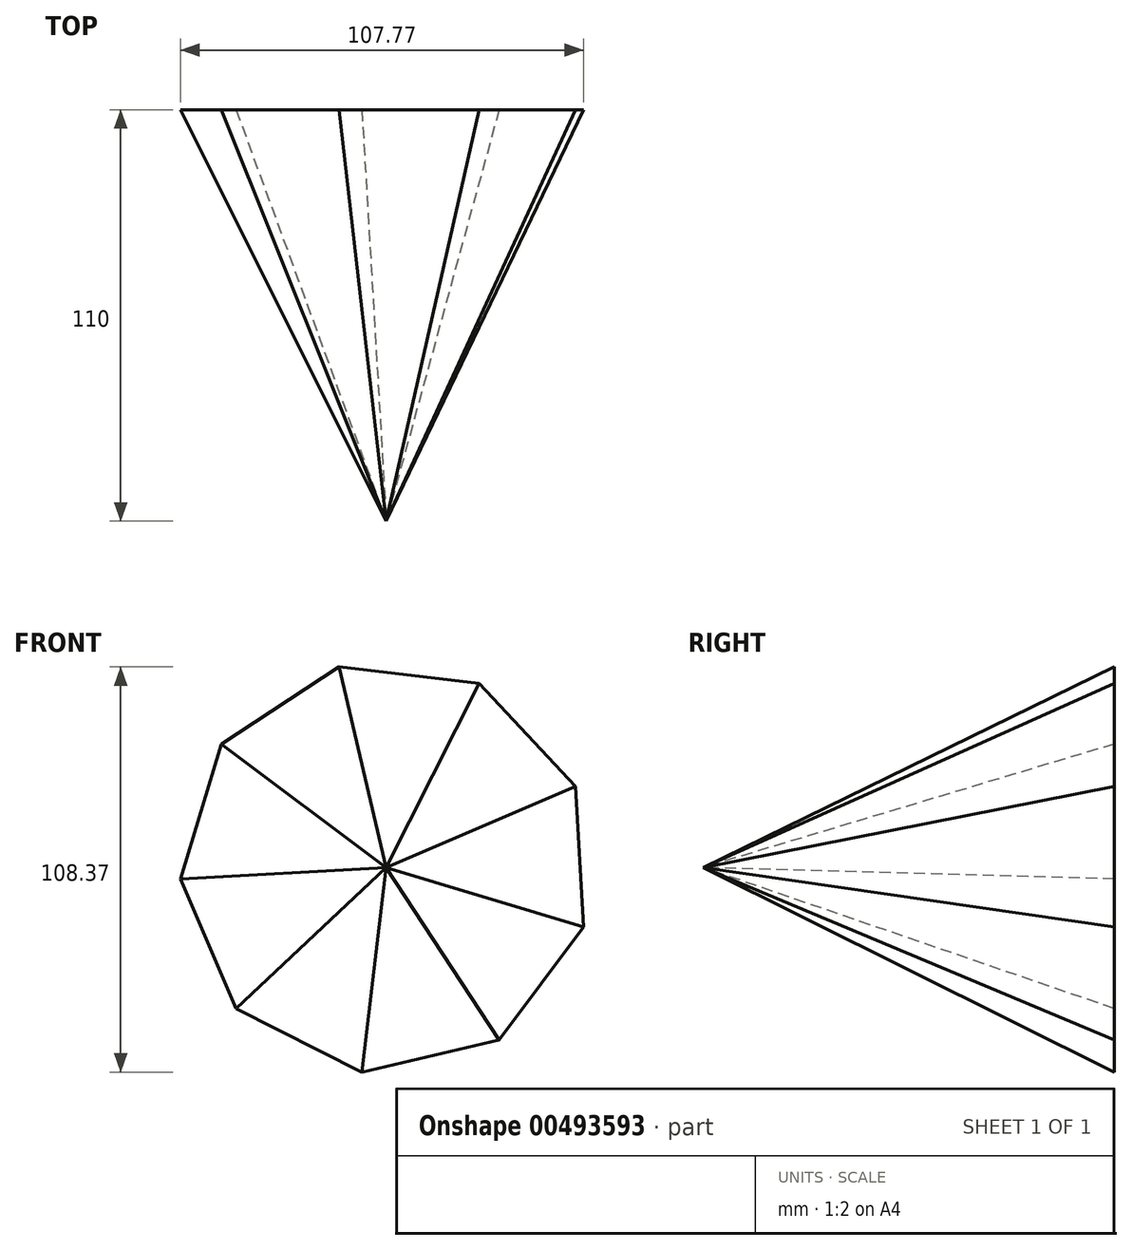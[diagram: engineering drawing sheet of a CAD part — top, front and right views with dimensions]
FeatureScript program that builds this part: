
annotation { "Feature Type Name" : "Feature", "Feature Type Description" : "" }
export const myFeature = defineFeature(function(context is Context, id is Id, definition is map)
    precondition{}
    {
        {
            var Q0;
            Q0=qCreatedBy(makeId("Front.planeOp"),FACE);
            var sketch = newSketch(context, id + "F0", { "sketchPlane" : qUnion([Q0])});
            skCircle(sketch, "E0.cCircle", {"center": v(0, 0) * mm, "radius": 55.1 * mm, "construction": true});
            skLineSegment(sketch, "E0.0", {"start": v(-40.16, -37.73) * mm, "end": v(-55.02, -3.08) * mm});
            skLineSegment(sketch, "E0.1", {"start": v(-55.02, -3.08) * mm, "end": v(-44.13, 33) * mm});
            skLineSegment(sketch, "E0.2", {"start": v(-44.13, 33) * mm, "end": v(-12.59, 53.65) * mm});
            skLineSegment(sketch, "E0.3", {"start": v(-12.59, 53.65) * mm, "end": v(24.84, 49.19) * mm});
            skLineSegment(sketch, "E0.4", {"start": v(24.84, 49.19) * mm, "end": v(50.64, 21.71) * mm});
            skLineSegment(sketch, "E0.5", {"start": v(50.64, 21.71) * mm, "end": v(52.75, -15.92) * mm});
            skLineSegment(sketch, "E0.6", {"start": v(52.75, -15.92) * mm, "end": v(30.18, -46.1) * mm});
            skLineSegment(sketch, "E0.7", {"start": v(30.18, -46.1) * mm, "end": v(-6.52, -54.72) * mm});
            skLineSegment(sketch, "E0.8", {"start": v(-6.52, -54.72) * mm, "end": v(-40.16, -37.73) * mm});
            skSolve(sketch);
        }
        {
            var Q0;
            Q0=qCreatedBy(makeId("Front.planeOp"),FACE);
            cPlane(context, id + "F1", {"entities" : qUnion([Q0]), "cplaneType" : CPlaneType.OFFSET, "offset" : 110 * mm, "width" : 150 * mm, "height" : 150 * mm});
        }
        {
            var Q0;
            Q0=qCreatedBy(id+"F1.planeOp",FACE);
            var sketch = newSketch(context, id + "F2", { "sketchPlane" : qUnion([Q0])});
            skPoint(sketch, "E1", {"position": v(0, 0) * mm});
            skSolve(sketch);
        }
        {
            var Q0;
            Q0=makeQuery(id+"F0.imprint","IMPRINT",FACE,{"disambiguationData":[TD([[makeQuery(id+"F0.imprint","IMPRINT",EDGE,{"derivedFrom":sQuery(id+"F0.wireOp",EDGE,"E0.0")}),-1.0]])]});
            var Q1;
            Q1=sQuery(id+"F2.wireOp",VERTEX,"E1");
            loft(context, id + "F3", {"sheetProfilesArray" : [{ "sheetProfileEntities" : qUnion([Q0]) }, { "sheetProfileEntities" : qUnion([Q1]) }]});
        }
    });
